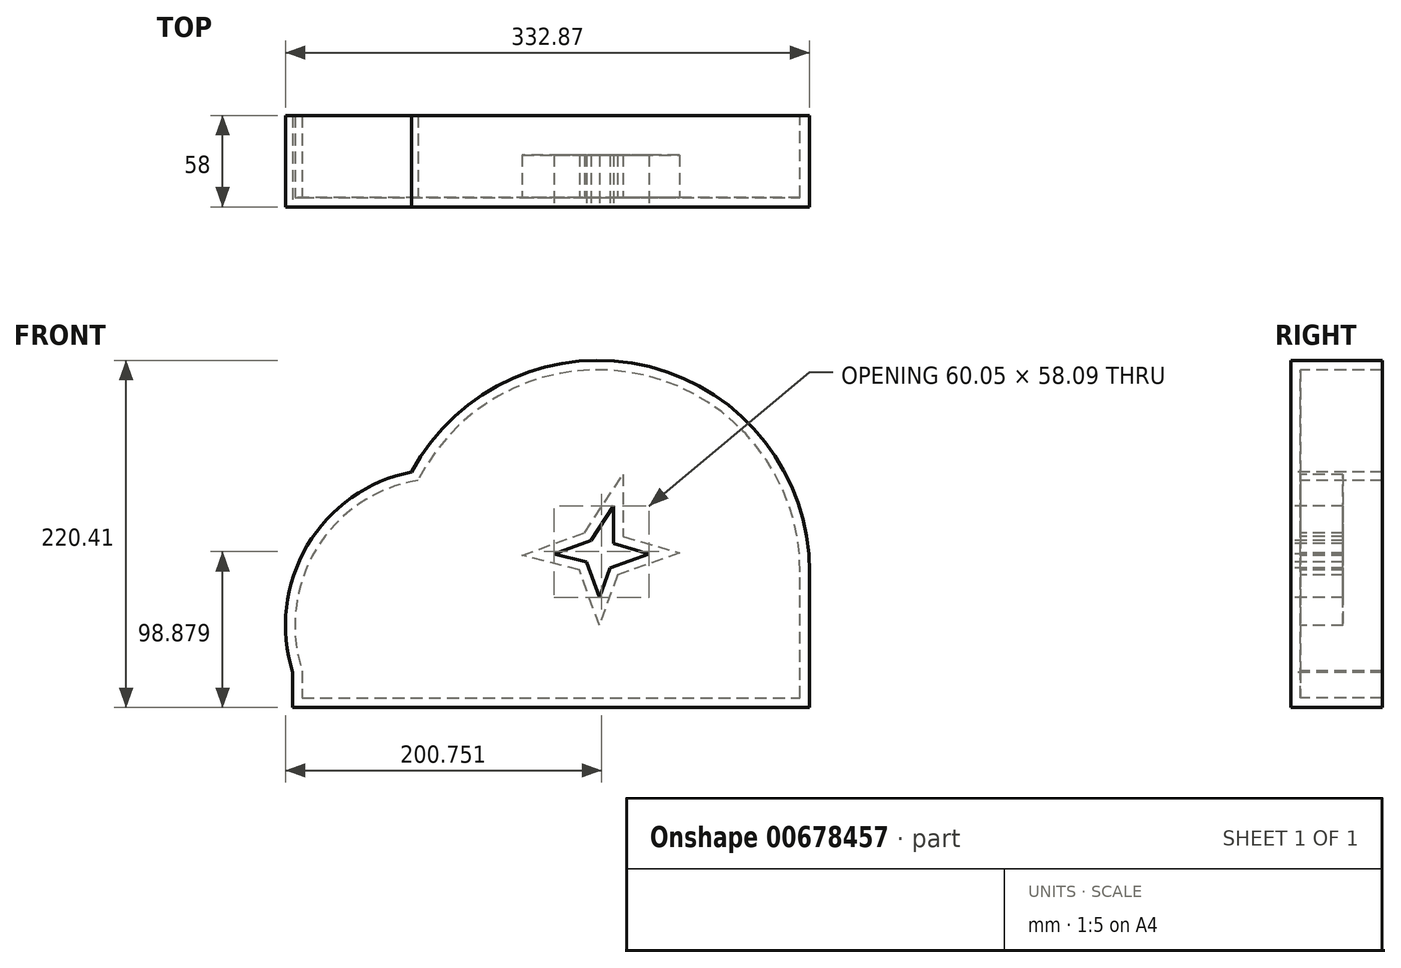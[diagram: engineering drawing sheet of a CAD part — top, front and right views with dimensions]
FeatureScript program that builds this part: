
annotation { "Feature Type Name" : "Feature", "Feature Type Description" : "" }
export const myFeature = defineFeature(function(context is Context, id is Id, definition is map)
    precondition{}
    {
        {
            var Q0;
            Q0=qCreatedBy(makeId("Front.planeOp"),FACE);
            var sketch = newSketch(context, id + "F0", { "sketchPlane" : qUnion([Q0])});
            skLineSegment(sketch, "E0", {"start": v(-196.33, -76) * mm, "end": v(-196.33, -98.13) * mm});
            skLineSegment(sketch, "E1", {"start": v(-196.33, -98.13) * mm, "end": v(131.93, -98.13) * mm});
            skLineSegment(sketch, "E2", {"start": v(131.93, -98.13) * mm, "end": v(131.93, -12.07) * mm});
            skLineSegment(sketch, "E3", {"start": v(7.46, 29.8) * mm, "end": v(7.46, 5.85) * mm});
            skLineSegment(sketch, "E4", {"start": v(7.46, 5.85) * mm, "end": v(29.84, -0.57) * mm});
            skLineSegment(sketch, "E5", {"start": v(29.84, -0.57) * mm, "end": v(5.16, -9.5) * mm});
            skLineSegment(sketch, "E6", {"start": v(5.16, -9.5) * mm, "end": v(-1.56, -28.3) * mm});
            skLineSegment(sketch, "E7", {"start": v(-1.56, -28.3) * mm, "end": v(-9.71, -5.75) * mm});
            skLineSegment(sketch, "E8", {"start": v(-9.71, -5.75) * mm, "end": v(-30.22, -0.57) * mm});
            skLineSegment(sketch, "E9", {"start": v(-30.22, -0.57) * mm, "end": v(-6.96, 7.84) * mm});
            skLineSegment(sketch, "E10", {"start": v(-6.96, 7.84) * mm, "end": v(7.46, 29.8) * mm});
            skArc(sketch, "E11", {"start": v(131.93, -12.07) * mm, "mid": v(24, 119.65) * mm, "end": v(-126.37, 39.76) * mm});
            skArc(sketch, "E12", {"start": v(-103.27, 53.28) * mm, "mid": v(-182.22, 11.98) * mm, "end": v(-196.33, -76) * mm});
            skPoint(sketch, "E13", {"position": v(-96.8, -19.4) * mm});
            skPoint(sketch, "E14", {"position": v(183.63, 127.58) * mm});
            skSolve(sketch);
        }
        {
            var Q0;
            Q0=qSketchRegion(id+"F0",true);
            extrude(context, id + "F1", {"entities" : qUnion([Q0]), "endBound" : BoundingType.SYMMETRIC, "oppositeDirection" : true, "depth" : 58 * mm, "offsetDistance" : 25 * mm});
        }
        {
            var Q0;
            Q0=makeQuery(id+"F1.opExtrude","CAP_FACE",FACE,{"disambiguationData":[OSD([sQuery(id+"F0.wireOp",EDGE,"E0"),sQuery(id+"F0.wireOp",EDGE,"E1"),sQuery(id+"F0.wireOp",EDGE,"E2"),sQuery(id+"F0.wireOp",EDGE,"XPoTxOzc-Mtjb-R9DS-EVyu-WJMlmXTQ7OyU"),sQuery(id+"F0.wireOp",EDGE,"07QTSwYt-StF0-8OgM-2wos-458a4vCQW62T")])],"isStart":false});
            shell(context, id + "F2", {"entities" : qUnion([Q0]), "thickness" : 6 * mm});
        }
        {
            var Q0;
            Q0=makeQuery(id+"F1.opExtrude","CAP_FACE",FACE,{"disambiguationData":[OSD([sQuery(id+"F0.wireOp",EDGE,"E0"),sQuery(id+"F0.wireOp",EDGE,"E1"),sQuery(id+"F0.wireOp",EDGE,"E2"),sQuery(id+"F0.wireOp",EDGE,"XPoTxOzc-Mtjb-R9DS-EVyu-WJMlmXTQ7OyU"),sQuery(id+"F0.wireOp",EDGE,"07QTSwYt-StF0-8OgM-2wos-458a4vCQW62T"),sQuery(id+"F0.wireOp",EDGE,"E3"),sQuery(id+"F0.wireOp",EDGE,"E4"),sQuery(id+"F0.wireOp",EDGE,"E5"),sQuery(id+"F0.wireOp",EDGE,"E6"),sQuery(id+"F0.wireOp",EDGE,"E7"),sQuery(id+"F0.wireOp",EDGE,"E8"),sQuery(id+"F0.wireOp",EDGE,"E9"),sQuery(id+"F0.wireOp",EDGE,"E10")])],"isStart":false});
            extrude(context, id + "F3", {"entities" : qUnion([Q0]), "operationType" : NewBodyOperationType.REMOVE, "oppositeDirection" : true, "depth" : 25 * mm, "offsetDistance" : 25 * mm});
        }
    });
